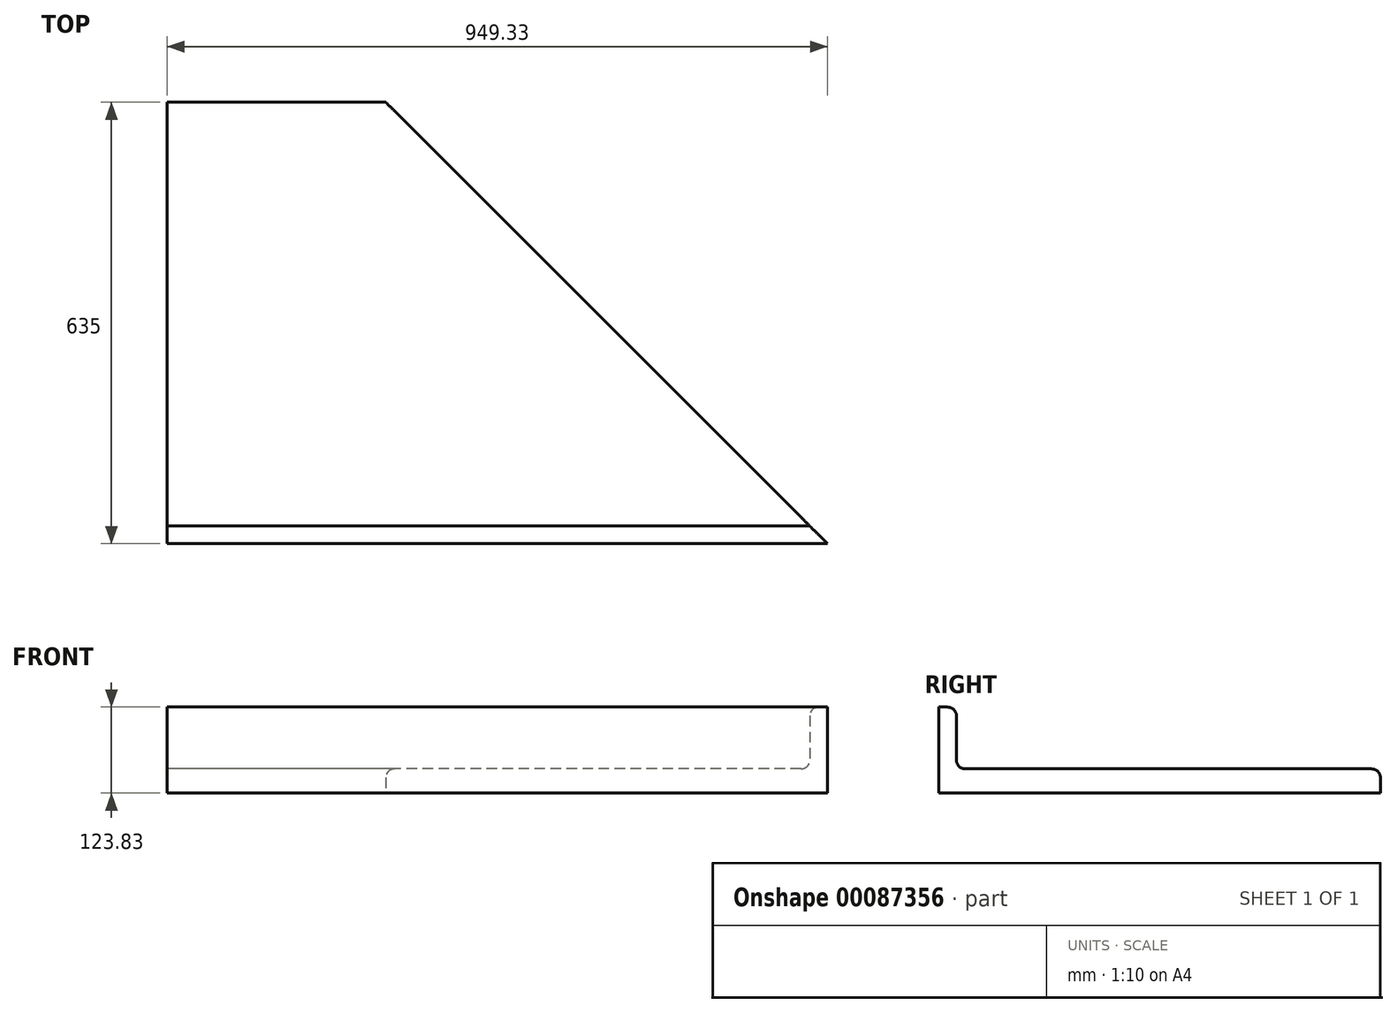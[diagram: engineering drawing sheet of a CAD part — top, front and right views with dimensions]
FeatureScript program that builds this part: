
annotation { "Feature Type Name" : "Feature", "Feature Type Description" : "" }
export const myFeature = defineFeature(function(context is Context, id is Id, definition is map)
    precondition{}
    {
        {
            var Q0;
            Q0=qCreatedBy(makeId("Right.planeOp"),FACE);
            var sketch = newSketch(context, id + "F0", { "sketchPlane" : qUnion([Q0])});
            skLineSegment(sketch, "E0.bottom", {"start": v(0, 0) * mm, "end": v(635, 0) * mm});
            skLineSegment(sketch, "E0.left", {"start": v(0, 0) * mm, "end": v(0, 34.93) * mm});
            skLineSegment(sketch, "E0.right", {"start": v(635, 0) * mm, "end": v(635, 22.22) * mm});
            skLineSegment(sketch, "E1.top", {"start": v(0, 123.82) * mm, "end": v(12.7, 123.82) * mm});
            skLineSegment(sketch, "E1.left", {"start": v(0, 34.92) * mm, "end": v(0, 123.82) * mm});
            skLineSegment(sketch, "E1.right", {"start": v(25.4, 47.62) * mm, "end": v(25.4, 111.12) * mm});
            skPoint(sketch, "E2.visualSharp", {"position": v(25.4, 123.82) * mm});
            skArc(sketch, "E2.filletArc", {"start": v(25.4, 111.12) * mm, "mid": v(21.68, 120.1) * mm, "end": v(12.7, 123.82) * mm});
            skLineSegment(sketch, "E3", {"start": v(622.3, 34.93) * mm, "end": v(38.1, 34.92) * mm});
            skPoint(sketch, "E4.visualSharp", {"position": v(25.4, 34.92) * mm});
            skArc(sketch, "E4.filletArc", {"start": v(25.4, 47.62) * mm, "mid": v(29.12, 38.64) * mm, "end": v(38.1, 34.92) * mm});
            skPoint(sketch, "E5.visualSharp", {"position": v(635, 34.93) * mm});
            skArc(sketch, "E5.filletArc", {"start": v(635, 22.22) * mm, "mid": v(631.28, 31.2) * mm, "end": v(622.3, 34.93) * mm});
            skSolve(sketch);
        }
        {
            var Q0;
            Q0=makeQuery(id+"F0.imprint","IMPRINT",FACE,{"disambiguationData":[TD([[makeQuery(id+"F0.imprint","IMPRINT",EDGE,{"derivedFrom":sQuery(id+"F0.wireOp",EDGE,"E0.bottom")}),1.0]])]});
            extrude(context, id + "F1", {"entities" : qUnion([Q0]), "depth" : 949.32 * mm});
        }
        {
            var Q0;
            Q0=makeQuery(id+"F1.opExtrude","SWEPT_FACE",FACE,{"disambiguationData":[OSD([sQuery(id+"F0.wireOp",EDGE,"E0.bottom")])]});
            var sketch = newSketch(context, id + "F2", { "sketchPlane" : qUnion([Q0])});
            skLineSegment(sketch, "E6", {"start": v(949.33, 0) * mm, "end": v(314.33, -635) * mm});
            skLineSegment(sketch, "E7", {"start": v(314.33, -635) * mm, "end": v(949.33, -635) * mm});
            skLineSegment(sketch, "E8", {"start": v(949.33, -635) * mm, "end": v(949.33, 0) * mm});
            skSolve(sketch);
        }
        {
            var Q0;
            Q0=makeQuery(id+"F2.imprint","IMPRINT",FACE,{"disambiguationData":[TD([[makeQuery(id+"F2.imprint","IMPRINT",EDGE,{"derivedFrom":sQuery(id+"F2.wireOp",EDGE,"E6")}),1.0]])]});
            extrude(context, id + "F3", {"entities" : qUnion([Q0]), "operationType" : NewBodyOperationType.REMOVE, "oppositeDirection" : true, "depth" : 254 * mm});
        }
    });
